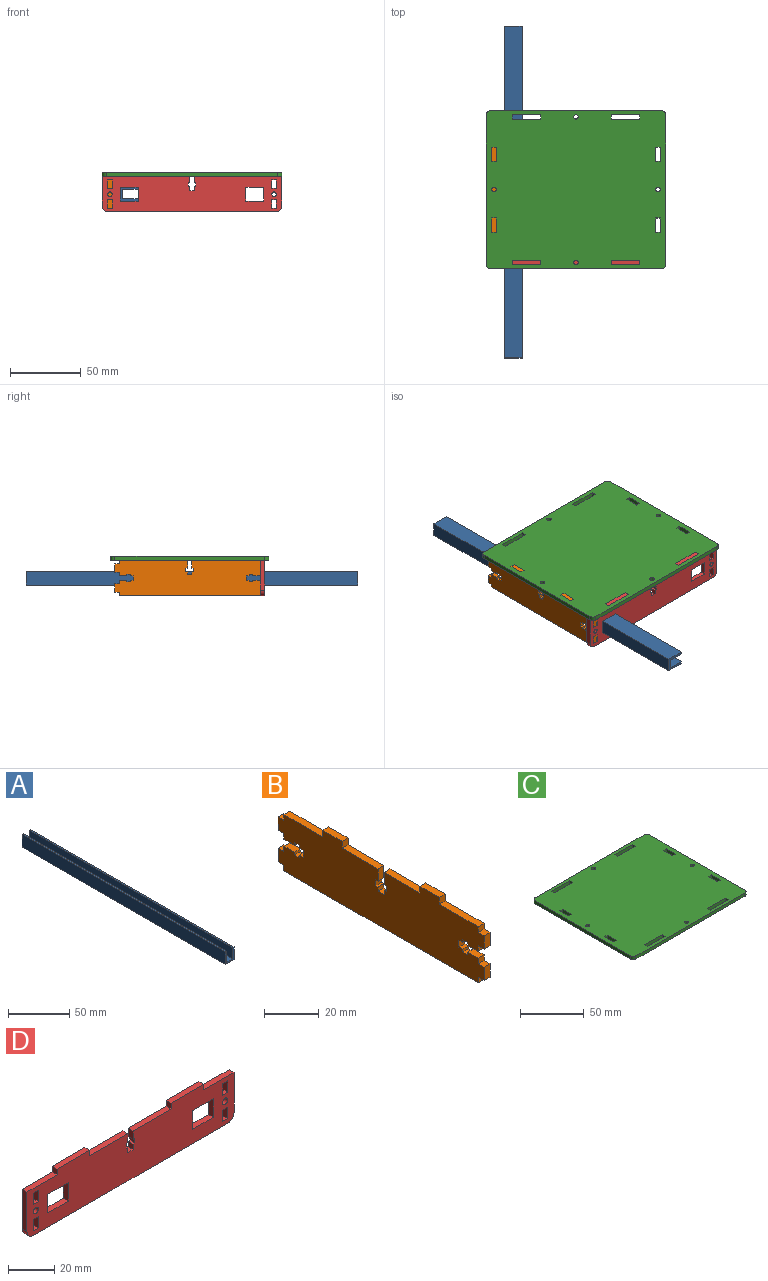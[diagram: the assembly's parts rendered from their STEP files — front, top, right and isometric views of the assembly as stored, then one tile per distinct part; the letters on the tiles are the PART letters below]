
ASSEMBLY  parts=4 mates=8
PART A: 10 faces, bbox 9.9x235x12.7 mm
  f0: plane 234.95x12.68mm, normal (-1,0,0), area 2979.2mm2, adj f1,f7,f8,f9
  f1: plane 234.95x9.89mm, normal (0,0,-1), area 2323.7mm2, adj f0,f2,f8,f9
  f2: plane 234.95x12.68mm, normal (1,0,0), area 2979.2mm2, adj f1,f3,f8,f9
  f3: plane 234.95x1.61mm, normal (0,0,1), area 378.3mm2, adj f2,f4,f8,f9
  f4: plane 234.95x11.07mm, normal (-1,0,0), area 2600.9mm2, adj f3,f5,f8,f9
  f5: plane 234.95x6.67mm, normal (0,0,1), area 1567.1mm2, adj f4,f6,f8,f9
  f6: plane 234.95x11.07mm, normal (1,0,0), area 2600.9mm2, adj f5,f7,f8,f9
  f7: plane 234.95x1.61mm, normal (0,0,1), area 378.3mm2, adj f0,f6,f8,f9
  f8: plane 12.68x9.89mm, normal (0,-1,0), area 51.6mm2, adj f0,f1,f2,f3,f4,f5,f6,f7
  f9: plane 12.68x9.89mm, normal (0,1,0), area 51.6mm2, adj f0,f1,f2,f3,f4,f5,f6,f7
PART B: 66 faces, bbox 3.1x106x28 mm
  f0: plane 18.45x3.05mm, normal (0,0,1), area 56.3mm2, adj f5,f14,f37,f63
  f1: plane 20x3.05mm, normal (0,0,1), area 61mm2, adj f5,f9,f14,f60
  f2: plane 3.05x2.45mm, normal (0,1,0), area 7.5mm2, adj f5,f14,f24,f49
  f3: plane 3.05x2.45mm, normal (0,-1,0), area 7.5mm2, adj f5,f14,f17,f47
  f4: plane 18.45x3.05mm, normal (0,0,1), area 56.3mm2, adj f5,f14,f27,f61
  f5: plane 106x28mm, normal (1,0,0), area 2521.8mm2, adj f0,f1,f2,f3,f4,f6,f7,f8
  f6: plane 3.05x2.5mm, normal (0,1,0), area 7.6mm2, adj f5,f12,f14,f26
  f7: plane 3.05x2.45mm, normal (0,1,0), area 7.5mm2, adj f5,f14,f21,f57
  f8: plane 3.05x2.45mm, normal (0,-1,0), area 7.5mm2, adj f5,f14,f19,f38
  f9: plane 3.05x2.5mm, normal (0,-1,0), area 7.6mm2, adj f1,f5,f14,f15
  f10: plane 100x3.05mm, normal (0,0,-1), area 305mm2, adj f5,f11,f13,f14
  f11: plane 3.05x2.5mm, normal (0,1,0), area 7.6mm2, adj f5,f10,f14,f22
  f12: plane 20x3.05mm, normal (0,0,1), area 61mm2, adj f5,f6,f14,f64
  f13: plane 3.05x2.5mm, normal (0,-1,0), area 7.6mm2, adj f5,f10,f14,f18
  f14: plane 106x28mm, normal (-1,0,0), area 2521.7mm2, adj f0,f1,f2,f3,f4,f6,f7,f8
  f15: plane 3.05x3mm, normal (0,0,1), area 9.2mm2, adj f5,f9,f14,f16
  f16: plane 6x3.05mm, normal (0,-1,0), area 18.3mm2, adj f5,f14,f15,f17
  f17: plane 3.05x3mm, normal (0,0,-1), area 9.2mm2, adj f3,f5,f14,f16
  f18: plane 3.05x3mm, normal (0,0,-1), area 9.2mm2, adj f5,f13,f14,f20
  f19: plane 3.05x3mm, normal (0,0,1), area 9.2mm2, adj f5,f8,f14,f20
  f20: plane 6x3.05mm, normal (0,-1,0), area 18.3mm2, adj f5,f14,f18,f19
  f21: plane 3.05x3mm, normal (0,0,1), area 9.2mm2, adj f5,f7,f14,f23
  f22: plane 3.05x3mm, normal (0,0,-1), area 9.2mm2, adj f5,f11,f14,f23
  f23: plane 6x3.05mm, normal (0,1,0), area 18.3mm2, adj f5,f14,f21,f22
  f24: plane 3.05x3mm, normal (0,0,-1), area 9.2mm2, adj f2,f5,f14,f25
  f25: plane 6x3.05mm, normal (0,1,0), area 18.3mm2, adj f5,f14,f24,f26
  f26: plane 3.05x3mm, normal (0,0,1), area 9.2mm2, adj f5,f6,f14,f25
  f27: plane 5.5x3.05mm, normal (0,1,0), area 16.8mm2, adj f4,f5,f14,f28
  f28: plane 3.05x1.15mm, normal (0,0,-1), area 3.5mm2, adj f5,f14,f27,f29
  f29: plane 3.05x2.5mm, normal (0,1,0), area 7.6mm2, adj f5,f14,f28,f30
  f30: plane 3.05x1.15mm, normal (0,0,1), area 3.5mm2, adj f5,f14,f29,f31
  f31: plane 3.05x2mm, normal (0,1,0), area 6.1mm2, adj f5,f14,f30,f33
  f32: plane 3.05x2mm, normal (0,-1,0), area 6.1mm2, adj f5,f14,f33,f34
  f33: plane 3.1x3.05mm, normal (0,0,1), area 9.5mm2, adj f5,f14,f31,f32
  f34: plane 3.05x1.15mm, normal (0,0,1), area 3.5mm2, adj f5,f14,f32,f35
  f35: plane 3.05x2.5mm, normal (0,-1,0), area 7.6mm2, adj f5,f14,f34,f36
  f36: plane 3.05x1.15mm, normal (0,0,-1), area 3.5mm2, adj f5,f14,f35,f37
  f37: plane 5.5x3.05mm, normal (0,-1,0), area 16.8mm2, adj f0,f5,f14,f36
  f38: plane 5.5x3.05mm, normal (0,0,1), area 16.8mm2, adj f5,f8,f14,f39
  f39: plane 3.05x1.15mm, normal (0,1,0), area 3.5mm2, adj f5,f14,f38,f40
  f40: plane 3.05x2.5mm, normal (0,0,1), area 7.6mm2, adj f5,f14,f39,f41
  f41: plane 3.05x1.15mm, normal (0,-1,0), area 3.5mm2, adj f5,f14,f40,f42
  f42: plane 3.05x2mm, normal (0,0,1), area 6.1mm2, adj f5,f14,f41,f43
  f43: plane 3.1x3.05mm, normal (0,-1,0), area 9.5mm2, adj f5,f14,f42,f44
  f44: plane 3.05x2mm, normal (0,0,-1), area 6.1mm2, adj f5,f14,f43,f45
  f45: plane 3.05x1.15mm, normal (0,-1,0), area 3.5mm2, adj f5,f14,f44,f46
  f46: plane 3.05x2.5mm, normal (0,0,-1), area 7.6mm2, adj f5,f14,f45,f48
  f47: plane 5.5x3.05mm, normal (0,0,-1), area 16.8mm2, adj f3,f5,f14,f48
  f48: plane 3.05x1.15mm, normal (0,1,0), area 3.5mm2, adj f5,f14,f46,f47
  f49: plane 5.5x3.05mm, normal (0,0,-1), area 16.8mm2, adj f2,f5,f14,f50
  f50: plane 3.05x1.15mm, normal (0,-1,0), area 3.5mm2, adj f5,f14,f49,f51
  f51: plane 3.05x2.5mm, normal (0,0,-1), area 7.6mm2, adj f5,f14,f50,f52
  f52: plane 3.05x1.15mm, normal (0,1,0), area 3.5mm2, adj f5,f14,f51,f53
  f53: plane 3.05x2mm, normal (0,0,-1), area 6.1mm2, adj f5,f14,f52,f54
  f54: plane 3.1x3.05mm, normal (0,1,0), area 9.5mm2, adj f5,f14,f53,f55
  f55: plane 3.05x2mm, normal (0,0,1), area 6.1mm2, adj f5,f14,f54,f56
  f56: plane 3.05x1.15mm, normal (0,1,0), area 3.5mm2, adj f5,f14,f55,f58
  f57: plane 5.5x3.05mm, normal (0,0,1), area 16.8mm2, adj f5,f7,f14,f59
  f58: plane 3.05x2.5mm, normal (0,0,1), area 7.6mm2, adj f5,f14,f56,f59
  f59: plane 3.05x1.15mm, normal (0,-1,0), area 3.5mm2, adj f5,f14,f57,f58
  f60: plane 3.05x3mm, normal (0,-1,0), area 9.2mm2, adj f1,f5,f14,f62
  f61: plane 3.05x3mm, normal (0,1,0), area 9.2mm2, adj f4,f5,f14,f62
  f62: plane 10x3.05mm, normal (0,0,1), area 30.5mm2, adj f5,f14,f60,f61
  f63: plane 3.05x3mm, normal (0,-1,0), area 9.2mm2, adj f0,f5,f14,f65
  f64: plane 3.05x3mm, normal (0,1,0), area 9.2mm2, adj f5,f12,f14,f65
  f65: plane 10x3.05mm, normal (0,0,1), area 30.5mm2, adj f5,f14,f63,f64
PART C: 46 faces, bbox 127x112x3 mm
  f0: plane 127x112mm, normal (0,0,1), area 13819.1mm2, adj f2,f3,f4,f5,f6,f7,f8,f9
  f1: plane 127x112mm, normal (0,0,-1), area 13819.1mm2, adj f2,f3,f4,f5,f6,f7,f8,f9
  f2: plane 121x3mm, normal (0,-1,0), area 363mm2, adj f0,f1,f42,f45
  f3: plane 106x3mm, normal (1,0,0), area 318mm2, adj f0,f1,f42,f43
  f4: plane 121x3mm, normal (0,1,0), area 363mm2, adj f0,f1,f43,f44
  f5: plane 106x3mm, normal (-1,0,0), area 318mm2, adj f0,f1,f44,f45
  f6: plane 3.05x3mm, normal (0,-1,0), area 9.1mm2, adj f0,f1,f7,f8
  f7: plane 10x3mm, normal (-1,0,0), area 30mm2, adj f0,f1,f6,f9
  f8: plane 10x3mm, normal (1,0,0), area 30mm2, adj f0,f1,f6,f9
  f9: plane 3.05x3mm, normal (0,1,0), area 9.1mm2, adj f0,f1,f7,f8
  f10: plane 3.05x3mm, normal (1,0,0), area 9.1mm2, adj f0,f1,f11,f12
  f11: plane 20x3mm, normal (0,-1,0), area 60mm2, adj f0,f1,f10,f13
  f12: plane 20x3mm, normal (0,1,0), area 60mm2, adj f0,f1,f10,f13
  f13: plane 3.05x3mm, normal (-1,0,0), area 9.1mm2, adj f0,f1,f11,f12
  f14: plane 20x3mm, normal (0,-1,0), area 60mm2, adj f0,f1,f15,f16
  f15: plane 3.05x3mm, normal (-1,0,0), area 9.1mm2, adj f0,f1,f14,f17
  f16: plane 3.05x3mm, normal (1,0,0), area 9.1mm2, adj f0,f1,f14,f17
  f17: plane 20x3mm, normal (0,1,0), area 60mm2, adj f0,f1,f15,f16
  f18: plane 10x3mm, normal (1,0,0), area 30mm2, adj f0,f1,f19,f20
  f19: plane 3.05x3mm, normal (0,-1,0), area 9.1mm2, adj f0,f1,f18,f21
  f20: plane 3.05x3mm, normal (0,1,0), area 9.1mm2, adj f0,f1,f18,f21
  f21: plane 10x3mm, normal (-1,0,0), area 30mm2, adj f0,f1,f19,f20
  f22: plane 3.05x3mm, normal (0,1,0), area 9.1mm2, adj f0,f1,f23,f24
  f23: plane 10x3mm, normal (1,0,0), area 30mm2, adj f0,f1,f22,f25
  f24: plane 10x3mm, normal (-1,0,0), area 30mm2, adj f0,f1,f22,f25
  f25: plane 3.05x3mm, normal (0,-1,0), area 9.1mm2, adj f0,f1,f23,f24
  f26: plane 10x3mm, normal (-1,0,0), area 30mm2, adj f0,f1,f27,f28
  f27: plane 3.05x3mm, normal (0,1,0), area 9.1mm2, adj f0,f1,f26,f29
  f28: plane 3.05x3mm, normal (0,-1,0), area 9.1mm2, adj f0,f1,f26,f29
  f29: plane 10x3mm, normal (1,0,0), area 30mm2, adj f0,f1,f27,f28
  f30: plane 3.05x3mm, normal (1,0,0), area 9.1mm2, adj f0,f1,f31,f33
  f31: plane 20x3mm, normal (0,1,0), area 60mm2, adj f0,f1,f30,f32
  f32: plane 3.05x3mm, normal (-1,0,0), area 9.1mm2, adj f0,f1,f31,f33
  f33: plane 20x3mm, normal (0,-1,0), area 60mm2, adj f0,f1,f30,f32
  f34: plane 3.05x3mm, normal (-1,0,0), area 9.1mm2, adj f0,f1,f35,f36
  f35: plane 20x3mm, normal (0,1,0), area 60mm2, adj f0,f1,f34,f37
  f36: plane 20x3mm, normal (0,-1,0), area 60mm2, adj f0,f1,f34,f37
  f37: plane 3.05x3mm, normal (1,0,0), area 9.1mm2, adj f0,f1,f35,f36
  f38: cylinder r=1.57mm len=3.15mm, axis (0,0,1), area 29.7mm2, adj f0,f1
  f39: cylinder r=1.57mm len=3.15mm, axis (0,0,1), area 29.7mm2, adj f0,f1
  f40: cylinder r=1.57mm len=3.15mm, axis (0,0,1), area 29.7mm2, adj f0,f1
  f41: cylinder r=1.57mm len=3.15mm, axis (0,0,1), area 29.7mm2, adj f0,f1
  f42: cylinder r=3mm len=3mm, axis (0,0,1), area 14.1mm2, adj f0,f1,f2,f3
  f43: cylinder r=3mm len=3mm, axis (0,0,-1), area 14.1mm2, adj f0,f1,f3,f4
  f44: cylinder r=3mm len=3mm, axis (0,0,1), area 14.1mm2, adj f0,f1,f4,f5
  f45: cylinder r=3mm len=3mm, axis (0,0,-1), area 14.1mm2, adj f0,f1,f2,f5
PART D: 54 faces, bbox 127x3.1x28 mm
  f0: plane 127x28mm, normal (0,-1,0), area 2910.6mm2, adj f2,f3,f4,f5,f6,f7,f8,f9
  f1: plane 127x28mm, normal (0,1,0), area 2910.6mm2, adj f2,f3,f4,f5,f6,f7,f8,f9
  f2: plane 23.45x3.05mm, normal (0,0,1), area 71.5mm2, adj f0,f1,f18,f23
  f3: plane 23.45x3.05mm, normal (0,0,1), area 71.5mm2, adj f0,f1,f20,f32
  f4: plane 18.5x3.05mm, normal (0,0,1), area 56.4mm2, adj f0,f1,f16,f17
  f5: plane 119x3.05mm, normal (0,0,-1), area 362.9mm2, adj f0,f1,f52,f53
  f6: plane 21x3.05mm, normal (1,0,0), area 64.1mm2, adj f0,f1,f7,f52
  f7: plane 18.5x3.05mm, normal (0,0,1), area 56.4mm2, adj f0,f1,f6,f21
  f8: plane 9.89x3.05mm, normal (-1,0,0), area 30.2mm2, adj f0,f1,f9,f14
  f9: plane 12.68x3.05mm, normal (0,0,1), area 38.7mm2, adj f0,f1,f8,f10
  f10: plane 9.89x3.05mm, normal (1,0,0), area 30.2mm2, adj f0,f1,f9,f14
  f11: plane 12.68x3.05mm, normal (0,0,1), area 38.7mm2, adj f0,f1,f12,f15
  f12: plane 9.89x3.05mm, normal (1,0,0), area 30.2mm2, adj f0,f1,f11,f13
  f13: plane 12.68x3.05mm, normal (0,0,-1), area 38.7mm2, adj f0,f1,f12,f15
  f14: plane 12.68x3.05mm, normal (0,0,-1), area 38.7mm2, adj f0,f1,f8,f10
  f15: plane 9.89x3.05mm, normal (-1,0,0), area 30.2mm2, adj f0,f1,f11,f13
  f16: plane 21x3.05mm, normal (-1,0,0), area 64.1mm2, adj f0,f1,f4,f53
  f17: plane 3.05x3mm, normal (-1,0,0), area 9.2mm2, adj f0,f1,f4,f19
  f18: plane 3.05x3mm, normal (1,0,0), area 9.2mm2, adj f0,f1,f2,f19
  f19: plane 20x3.05mm, normal (0,0,1), area 61mm2, adj f0,f1,f17,f18
  f20: plane 3.05x3mm, normal (-1,0,0), area 9.2mm2, adj f0,f1,f3,f22
  f21: plane 3.05x3mm, normal (1,0,0), area 9.2mm2, adj f0,f1,f7,f22
  f22: plane 20x3.05mm, normal (0,0,1), area 61mm2, adj f0,f1,f20,f21
  f23: plane 4.5x3.05mm, normal (1,0,0), area 13.7mm2, adj f0,f1,f2,f24
  f24: plane 3.05x1.15mm, normal (0,0,-1), area 3.5mm2, adj f0,f1,f23,f25
  f25: plane 3.05x2.5mm, normal (1,0,0), area 7.6mm2, adj f0,f1,f24,f26
  f26: plane 3.05x1.15mm, normal (0,0,1), area 3.5mm2, adj f0,f1,f25,f27
  f27: plane 3.05x3mm, normal (1,0,0), area 9.2mm2, adj f0,f1,f26,f28
  f28: plane 3.1x3.05mm, normal (0,0,1), area 9.5mm2, adj f0,f1,f27,f29
  f29: plane 3.05x3mm, normal (-1,0,0), area 9.2mm2, adj f0,f1,f28,f30
  f30: plane 3.05x1.15mm, normal (0,0,1), area 3.5mm2, adj f0,f1,f29,f31
  f31: plane 3.05x2.5mm, normal (-1,0,0), area 7.6mm2, adj f0,f1,f30,f33
  f32: plane 4.5x3.05mm, normal (-1,0,0), area 13.7mm2, adj f0,f1,f3,f33
  f33: plane 3.05x1.15mm, normal (0,0,-1), area 3.5mm2, adj f0,f1,f31,f32
  f34: plane 6x3.05mm, normal (-1,0,0), area 18.3mm2, adj f0,f1,f35,f36
  f35: plane 3.1x3.05mm, normal (0,0,1), area 9.5mm2, adj f0,f1,f34,f37
  f36: plane 3.1x3.05mm, normal (0,0,-1), area 9.5mm2, adj f0,f1,f34,f37
  f37: plane 6x3.05mm, normal (1,0,0), area 18.3mm2, adj f0,f1,f35,f36
  f38: plane 6x3.05mm, normal (1,0,0), area 18.3mm2, adj f0,f1,f39,f40
  f39: plane 3.1x3.05mm, normal (0,0,-1), area 9.5mm2, adj f0,f1,f38,f41
  f40: plane 3.1x3.05mm, normal (0,0,1), area 9.5mm2, adj f0,f1,f38,f41
  f41: plane 6x3.05mm, normal (-1,0,0), area 18.3mm2, adj f0,f1,f39,f40
  f42: plane 3.1x3.05mm, normal (0,0,1), area 9.5mm2, adj f0,f1,f43,f44
  f43: plane 6x3.05mm, normal (1,0,0), area 18.3mm2, adj f0,f1,f42,f45
  f44: plane 6x3.05mm, normal (-1,0,0), area 18.3mm2, adj f0,f1,f42,f45
  f45: plane 3.1x3.05mm, normal (0,0,-1), area 9.5mm2, adj f0,f1,f43,f44
  f46: plane 3.1x3.05mm, normal (0,0,-1), area 9.5mm2, adj f0,f1,f47,f48
  f47: plane 6x3.05mm, normal (-1,0,0), area 18.3mm2, adj f0,f1,f46,f49
  f48: plane 6x3.05mm, normal (1,0,0), area 18.3mm2, adj f0,f1,f46,f49
  f49: plane 3.1x3.05mm, normal (0,0,1), area 9.5mm2, adj f0,f1,f47,f48
  f50: cylinder r=1.57mm len=3.15mm, axis (0,-1,0), area 30.2mm2, adj f0,f1
  f51: cylinder r=1.57mm len=3.15mm, axis (0,-1,0), area 30.2mm2, adj f0,f1
  f52: cylinder r=4mm len=4mm, axis (0,-1,0), area 19.2mm2, adj f0,f1,f5,f6
  f53: cylinder r=4mm len=4mm, axis (0,1,0), area 19.2mm2, adj f0,f1,f5,f16
PLACE A rot(axis=(0,1,0),90deg) t=(-150.98,10.46,-8.1)mm
PLACE B t=(-158.21,12.03,-8.1)mm
PLACE C t=(-100.18,12.03,4.4)mm
PLACE D t=(-100.18,-39.5,-8.1)mm
MATE planar C.f29 <-> B.f14  axis (1,0,0) through (-159.73,-12.97,7.4)mm
MATE planar D.f2 <-> C.f1  axis (0,0,1) through (-113.46,-39.5,4.4)mm
MATE planar D.f0 <-> C.f12  axis (0,-1,0) through (-100.18,-41.02,-7.59)mm
MATE planar D.f10 <-> A.f1  axis (1,0,0) through (-150.98,-41.02,-8.1)mm
MATE planar C.f1 <-> B.f1  axis (0,0,-1) through (-100.18,12.03,4.4)mm
MATE planar C.f27 <-> B.f60  axis (0,1,0) through (-158.21,-17.97,4.4)mm
MATE planar D.f14 <-> A.f0  axis (0,0,-1) through (-144.64,-41.02,-3.16)mm
MATE planar C.f13 <-> D.f18  axis (-1,0,0) through (-125.18,-37.97,5.9)mm
